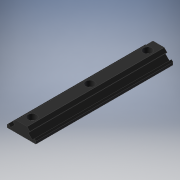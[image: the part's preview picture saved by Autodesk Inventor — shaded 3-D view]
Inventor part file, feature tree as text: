
AUTODESK INVENTOR PART (.ipt)
format: ipt  version: 2019 (Build 230136000, 136)  size: 146,944 bytes
history: native  units: mm
features: other x14, extrude x1, hole x1, pattern_linear x1, sketch x1
ambient origin geometry x8: Origin, YZ Plane, XZ Plane, XY Plane, X Axis, Y Axis, Z Axis, Center Point
bodies: Solid1 (feature_tree)
feature tree (18):
  extrude  "Extrusion1"  Depth=10.0mm TaperAngle=0.0deg
  hole  "Hole1"  [1 undecoded]
  pattern_linear  "Rectangular Pattern1"  [2 undecoded]
  other  "to_block_XY"
  other  "to_block_YZ"
  other  "to_block_ZX"
  other  "to_block_X"
  other  "to_block_Y"
  other  "to_block_Z"
  other  "to_block_Center"
  other  "to_block2_XY"
  other  "to_block2_YZ"
  other  "to_block2_ZX"
  other  "to_block2_X"
  other  "to_block2_Y"
  other  "to_block2_Z"
  other  "to_block2_Center"
  sketch  "Sketch2"  dims[d0=95.0mm d1=0.0mm d2=3.5mm d3=6.0mm d4=6.0mm d5=4.0mm d6=90.0deg d7=7.5mm d8=0.0mm d9=30.0mm d11=40.0mm d12=10.0mm d14=0.0mm]
note: 3 required parameter values undecoded (feature->parameter linkage not recoverable at this tier; creation-order binding heuristic only, values carry confidence <= 0.55)
